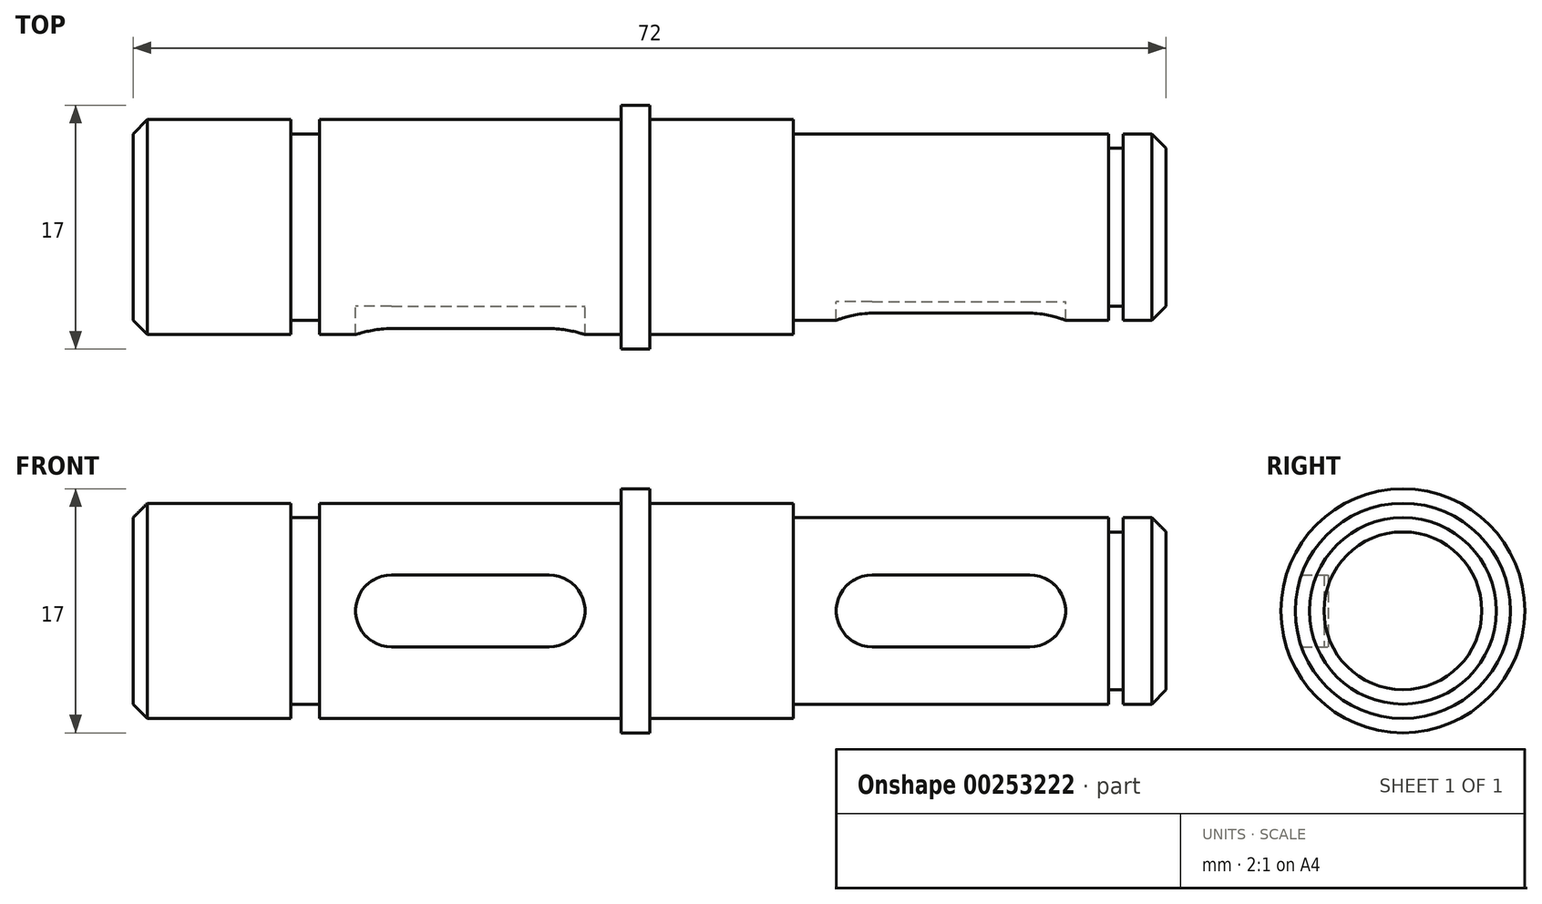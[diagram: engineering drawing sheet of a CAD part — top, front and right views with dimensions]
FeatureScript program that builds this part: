
annotation { "Feature Type Name" : "Feature", "Feature Type Description" : "" }
export const myFeature = defineFeature(function(context is Context, id is Id, definition is map)
    precondition{}
    {
        {
            var Q0;
            Q0=qCreatedBy(makeId("Front.planeOp"),FACE);
            var sketch = newSketch(context, id + "F0", { "sketchPlane" : qUnion([Q0])});
            skLineSegment(sketch, "E0", {"start": v(-48.93, 7.5) * mm, "end": v(-48.93, -7.5) * mm});
            skLineSegment(sketch, "E1", {"start": v(-27.93, 8.5) * mm, "end": v(-27.93, -8.5) * mm});
            skLineSegment(sketch, "E2", {"start": v(-48.93, -7.5) * mm, "end": v(-27.93, -7.5) * mm});
            skLineSegment(sketch, "E3", {"start": v(-48.93, 7.5) * mm, "end": v(-27.93, 7.5) * mm});
            skLineSegment(sketch, "E4", {"start": v(-48.93, 6.5) * mm, "end": v(-48.93, -6.5) * mm});
            skLineSegment(sketch, "E5", {"start": v(-48.93, 6.5) * mm, "end": v(-50.93, 6.5) * mm});
            skLineSegment(sketch, "E6", {"start": v(-50.93, 6.5) * mm, "end": v(-50.93, -6.5) * mm});
            skLineSegment(sketch, "E7", {"start": v(-50.93, -6.5) * mm, "end": v(-48.93, -6.5) * mm});
            skLineSegment(sketch, "E8", {"start": v(-50.93, 7.5) * mm, "end": v(-50.93, -7.5) * mm});
            skLineSegment(sketch, "E9", {"start": v(-50.93, -7.5) * mm, "end": v(-60.93, -7.5) * mm});
            skLineSegment(sketch, "E10", {"start": v(-60.93, -7.5) * mm, "end": v(-60.93, 7.5) * mm});
            skLineSegment(sketch, "E11", {"start": v(-60.93, 7.5) * mm, "end": v(-50.93, 7.5) * mm});
            skLineSegment(sketch, "E12", {"start": v(-60.93, -7.5) * mm, "end": v(-61.93, -6.5) * mm});
            skLineSegment(sketch, "E13", {"start": v(-61.93, -6.5) * mm, "end": v(-61.93, 0) * mm});
            skLineSegment(sketch, "E14.MirrorCS", {"start": v(-61.93, 6.5) * mm, "end": v(-61.93, 0) * mm});
            skLineSegment(sketch, "E15.MirrorCS", {"start": v(-60.93, 7.5) * mm, "end": v(-61.93, 6.5) * mm});
            skLineSegment(sketch, "E16", {"start": v(-24.93, 7.5) * mm, "end": v(-24.93, -7.5) * mm});
            skLineSegment(sketch, "E17", {"start": v(-24.93, 7.5) * mm, "end": v(-15.93, 7.5) * mm});
            skLineSegment(sketch, "E18", {"start": v(-15.93, 7.5) * mm, "end": v(-15.93, -7.5) * mm});
            skLineSegment(sketch, "E19", {"start": v(-15.93, -7.5) * mm, "end": v(-24.93, -7.5) * mm});
            skLineSegment(sketch, "E20", {"start": v(-15.93, 6.5) * mm, "end": v(-15.93, -6.5) * mm});
            skLineSegment(sketch, "E21", {"start": v(-15.93, -6.5) * mm, "end": v(6.07, -6.5) * mm});
            skLineSegment(sketch, "E22", {"start": v(6.07, -6.5) * mm, "end": v(6.07, 6.5) * mm});
            skLineSegment(sketch, "E23", {"start": v(6.07, 6.5) * mm, "end": v(-15.93, 6.5) * mm});
            skLineSegment(sketch, "E24", {"start": v(6.07, 5.5) * mm, "end": v(6.07, -5.5) * mm});
            skLineSegment(sketch, "E25", {"start": v(6.07, -5.5) * mm, "end": v(7.07, -5.5) * mm});
            skLineSegment(sketch, "E26", {"start": v(7.07, -5.5) * mm, "end": v(7.07, 5.5) * mm});
            skLineSegment(sketch, "E27", {"start": v(7.07, 5.5) * mm, "end": v(6.07, 5.5) * mm});
            skLineSegment(sketch, "E28", {"start": v(7.07, -5.5) * mm, "end": v(7.07, -6.5) * mm});
            skLineSegment(sketch, "E29", {"start": v(7.07, 5.5) * mm, "end": v(7.07, 6.5) * mm});
            skLineSegment(sketch, "E30", {"start": v(7.07, 6.5) * mm, "end": v(9.07, 6.5) * mm});
            skLineSegment(sketch, "E31", {"start": v(9.07, 6.5) * mm, "end": v(9.07, -6.5) * mm});
            skLineSegment(sketch, "E32", {"start": v(9.07, -6.5) * mm, "end": v(7.07, -6.5) * mm});
            skLineSegment(sketch, "E33", {"start": v(9.07, -6.5) * mm, "end": v(10.07, -5.5) * mm});
            skLineSegment(sketch, "E34", {"start": v(10.07, -5.5) * mm, "end": v(10.07, 0) * mm});
            skLineSegment(sketch, "E35.MirrorCS", {"start": v(10.07, 5.5) * mm, "end": v(10.07, 0) * mm});
            skLineSegment(sketch, "E36.MirrorCS", {"start": v(9.07, 6.5) * mm, "end": v(10.07, 5.5) * mm});
            skLineSegment(sketch, "E37", {"start": v(-27.93, 8.5) * mm, "end": v(-25.93, 8.5) * mm});
            skLineSegment(sketch, "E38", {"start": v(-25.93, 8.5) * mm, "end": v(-25.93, -8.5) * mm});
            skLineSegment(sketch, "E39", {"start": v(-25.93, -8.5) * mm, "end": v(-27.93, -8.5) * mm});
            skLineSegment(sketch, "E40", {"start": v(-24.93, -7.5) * mm, "end": v(-25.93, -7.5) * mm});
            skLineSegment(sketch, "E41", {"start": v(-24.93, 7.5) * mm, "end": v(-25.93, 7.5) * mm});
            skPoint(sketch, "E42", {"position": v(-38.43, 7.5) * mm});
            skPoint(sketch, "E43", {"position": v(-4.93, 6.5) * mm});
            skLineSegment(sketch, "E44", {"start": v(-4.93, 6.5) * mm, "end": v(-4.93, 10.81) * mm, "construction": true});
            skLineSegment(sketch, "E45", {"start": v(-38.43, 7.5) * mm, "end": v(-38.43, 12.22) * mm, "construction": true});
            skArc(sketch, "E46", {"start": v(-43.93, 2.5) * mm, "mid": v(-46.43, 0) * mm, "end": v(-43.93, -2.5) * mm});
            skArc(sketch, "E47.MirrorCS", {"start": v(-32.93, 2.5) * mm, "mid": v(-30.43, 0) * mm, "end": v(-32.93, -2.5) * mm});
            skLineSegment(sketch, "E48", {"start": v(-43.93, 2.5) * mm, "end": v(-32.93, 2.5) * mm});
            skLineSegment(sketch, "E49", {"start": v(-32.93, -2.5) * mm, "end": v(-43.93, -2.5) * mm});
            skArc(sketch, "E50", {"start": v(-10.43, 2.5) * mm, "mid": v(-12.93, 0) * mm, "end": v(-10.43, -2.5) * mm});
            skArc(sketch, "E51.MirrorCS", {"start": v(0.57, 2.5) * mm, "mid": v(3.07, 0) * mm, "end": v(0.57, -2.5) * mm});
            skLineSegment(sketch, "E52", {"start": v(-10.43, -2.5) * mm, "end": v(0.57, -2.5) * mm});
            skLineSegment(sketch, "E53", {"start": v(-10.43, 2.5) * mm, "end": v(0.57, 2.5) * mm});
            skLineSegment(sketch, "E54", {"start": v(-61.93, 0) * mm, "end": v(10.07, 0) * mm});
            skSolve(sketch);
        }
        {
            var Q0;
            {var subQ4=sQuery(id+"F0.wireOp",EDGE,"E35.MirrorCS");Q0=makeQuery(id+"F0.imprint","IMPRINT",FACE,{"disambiguationData":[TD([[makeQuery(id+"F0.imprint","IMPRINT",EDGE,{"derivedFrom":subQ4}),-1.0]])]});}
            var Q1;
            {var subQ4=sQuery(id+"F0.wireOp",EDGE,"E29");Q1=makeQuery(id+"F0.imprint","IMPRINT",FACE,{"disambiguationData":[TD([[makeQuery(id+"F0.imprint","IMPRINT",EDGE,{"derivedFrom":subQ4}),-1.0]])]});}
            var Q2;
            {var subQ0=sQuery(id+"F0.wireOp",EDGE,"E27");Q2=makeQuery(id+"F0.imprint","IMPRINT",FACE,{"disambiguationData":[TD([[makeQuery(id+"F0.imprint","IMPRINT",EDGE,{"derivedFrom":subQ0}),1.0]])]});}
            var Q3;
            {var subQ8=sQuery(id+"F0.wireOp",EDGE,"E23");Q3=makeQuery(id+"F0.imprint","IMPRINT",FACE,{"disambiguationData":[TD([[makeQuery(id+"F0.imprint","IMPRINT",EDGE,{"derivedFrom":subQ8}),1.0]])]});}
            var Q4;
            {var subQ0=sQuery(id+"F0.wireOp",EDGE,"E53");Q4=makeQuery(id+"F0.imprint","IMPRINT",FACE,{"disambiguationData":[TD([[makeQuery(id+"F0.imprint","IMPRINT",EDGE,{"derivedFrom":subQ0}),-1.0]])]});}
            var Q5;
            {var subQ5=sQuery(id+"F0.wireOp",EDGE,"E17");Q5=makeQuery(id+"F0.imprint","IMPRINT",FACE,{"disambiguationData":[TD([[makeQuery(id+"F0.imprint","IMPRINT",EDGE,{"derivedFrom":subQ5}),-1.0]])]});}
            var Q6;
            {var subQ0=sQuery(id+"F0.wireOp",EDGE,"E41");Q6=makeQuery(id+"F0.imprint","IMPRINT",FACE,{"disambiguationData":[TD([[makeQuery(id+"F0.imprint","IMPRINT",EDGE,{"derivedFrom":subQ0}),1.0]])]});}
            var Q7;
            {var subQ0=sQuery(id+"F0.wireOp",EDGE,"E37");Q7=makeQuery(id+"F0.imprint","IMPRINT",FACE,{"disambiguationData":[TD([[makeQuery(id+"F0.imprint","IMPRINT",EDGE,{"derivedFrom":subQ0}),-1.0]])]});}
            var Q8;
            {var subQ9=sQuery(id+"F0.wireOp",EDGE,"E3");Q8=makeQuery(id+"F0.imprint","IMPRINT",FACE,{"disambiguationData":[TD([[makeQuery(id+"F0.imprint","IMPRINT",EDGE,{"derivedFrom":subQ9}),-1.0]])]});}
            var Q9;
            {var subQ0=sQuery(id+"F0.wireOp",EDGE,"E48");Q9=makeQuery(id+"F0.imprint","IMPRINT",FACE,{"disambiguationData":[TD([[makeQuery(id+"F0.imprint","IMPRINT",EDGE,{"derivedFrom":subQ0}),-1.0]])]});}
            var Q10;
            {var subQ0=sQuery(id+"F0.wireOp",EDGE,"E5");Q10=makeQuery(id+"F0.imprint","IMPRINT",FACE,{"disambiguationData":[TD([[makeQuery(id+"F0.imprint","IMPRINT",EDGE,{"derivedFrom":subQ0}),1.0]])]});}
            var Q11;
            {var subQ0=sQuery(id+"F0.wireOp",EDGE,"E11");Q11=makeQuery(id+"F0.imprint","IMPRINT",FACE,{"disambiguationData":[TD([[makeQuery(id+"F0.imprint","IMPRINT",EDGE,{"derivedFrom":subQ0}),-1.0]])]});}
            var Q12;
            {var subQ4=sQuery(id+"F0.wireOp",EDGE,"E14.MirrorCS");Q12=makeQuery(id+"F0.imprint","IMPRINT",FACE,{"disambiguationData":[TD([[makeQuery(id+"F0.imprint","IMPRINT",EDGE,{"derivedFrom":subQ4}),1.0]])]});}
            var Q13;
            Q13=sQuery(id+"F0.wireOp",EDGE,"E54");
            revolve(context, id + "F1", {"entities" : qUnion([Q0, Q1, Q2, Q3, Q4, Q5, Q6, Q7, Q8, Q9, Q10, Q11, Q12]), "axis" : qUnion([Q13]), "revolveType" : RevolveType.FULL});
        }
        {
            var Q0;
            {var subQ0=sQuery(id+"F0.wireOp",EDGE,"E49");Q0=makeQuery(id+"F0.imprint","IMPRINT",FACE,{"disambiguationData":[TD([[makeQuery(id+"F0.imprint","IMPRINT",EDGE,{"derivedFrom":subQ0}),-1.0]])]});}
            var Q1;
            {var subQ0=sQuery(id+"F0.wireOp",EDGE,"E48");Q1=makeQuery(id+"F0.imprint","IMPRINT",FACE,{"disambiguationData":[TD([[makeQuery(id+"F0.imprint","IMPRINT",EDGE,{"derivedFrom":subQ0}),-1.0]])]});}
            var Q2;
            {var subQ0=sQuery(id+"F0.wireOp",EDGE,"E53");Q2=makeQuery(id+"F0.imprint","IMPRINT",FACE,{"disambiguationData":[TD([[makeQuery(id+"F0.imprint","IMPRINT",EDGE,{"derivedFrom":subQ0}),-1.0]])]});}
            var Q3;
            {var subQ0=sQuery(id+"F0.wireOp",EDGE,"E52");Q3=makeQuery(id+"F0.imprint","IMPRINT",FACE,{"disambiguationData":[TD([[makeQuery(id+"F0.imprint","IMPRINT",EDGE,{"derivedFrom":subQ0}),1.0]])]});}
            extrude(context, id + "F2", {"entities" : qUnion([Q0, Q1, Q2, Q3]), "operationType" : NewBodyOperationType.REMOVE, "depth" : 25 * mm});
        }
        {
            var Q0;
            Q0=makeQuery(id+"F2.boolean.opBoolean","COPY",FACE,{"derivedFrom":makeQuery(id+"F2.opExtrude","CAP_FACE",FACE,{"disambiguationData":[OSD([sQuery(id+"F0.wireOp",EDGE,"E46"),sQuery(id+"F0.wireOp",EDGE,"E47.MirrorCS"),sQuery(id+"F0.wireOp",EDGE,"E48"),sQuery(id+"F0.wireOp",EDGE,"E49")])],"isStart":true})});
            extrude(context, id + "F3", {"entities" : qUnion([Q0]), "operationType" : NewBodyOperationType.ADD, "depth" : 5.5 * mm});
        }
        {
            var Q0;
            Q0=makeQuery(id+"F2.boolean.opBoolean","COPY",FACE,{"derivedFrom":makeQuery(id+"F2.opExtrude","CAP_FACE",FACE,{"disambiguationData":[OSD([sQuery(id+"F0.wireOp",EDGE,"E50"),sQuery(id+"F0.wireOp",EDGE,"E51.MirrorCS"),sQuery(id+"F0.wireOp",EDGE,"E52"),sQuery(id+"F0.wireOp",EDGE,"E53")])],"isStart":true})});
            extrude(context, id + "F4", {"entities" : qUnion([Q0]), "operationType" : NewBodyOperationType.ADD, "depth" : 5.2 * mm});
        }
    });
